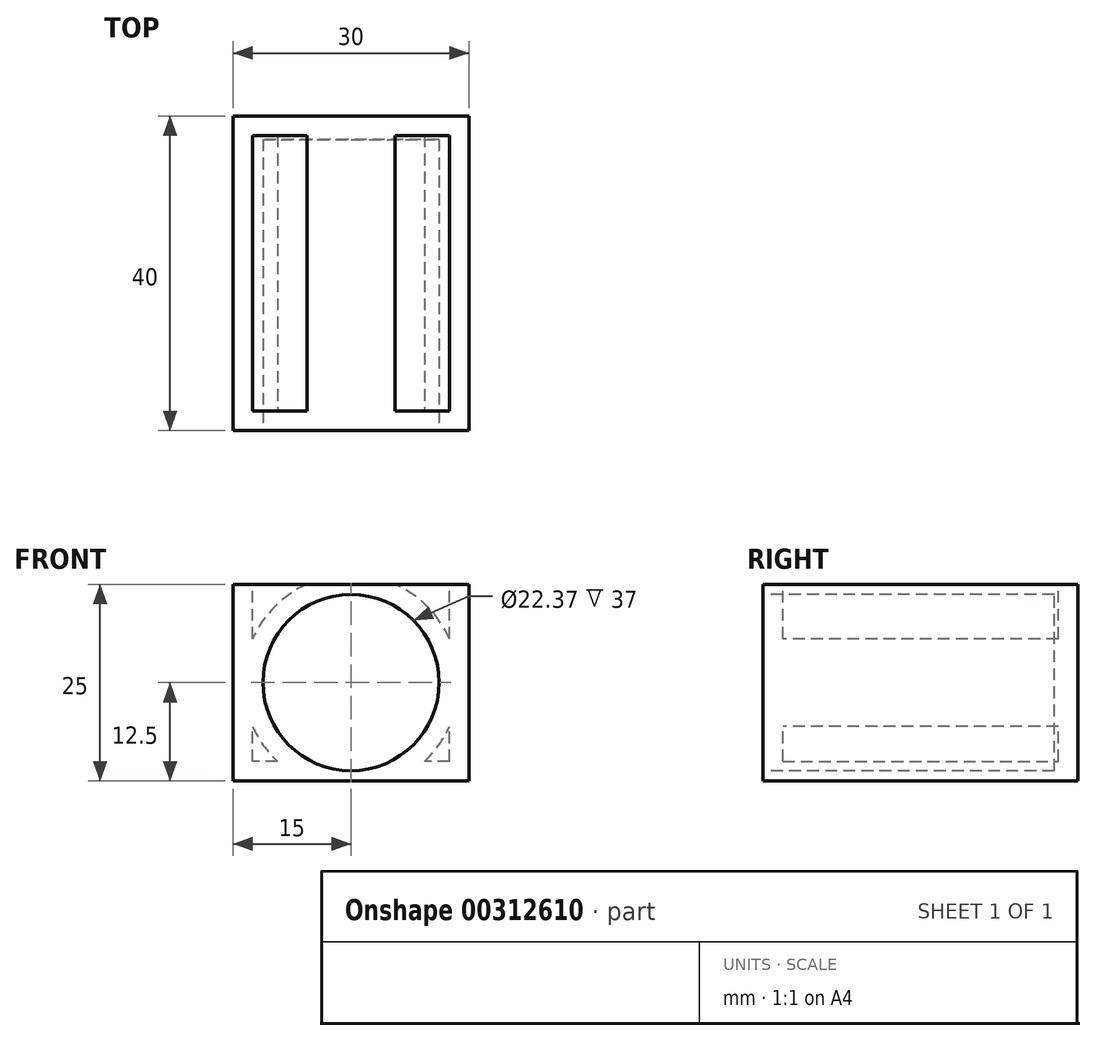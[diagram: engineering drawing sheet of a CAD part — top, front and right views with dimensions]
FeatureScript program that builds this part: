
annotation { "Feature Type Name" : "Feature", "Feature Type Description" : "" }
export const myFeature = defineFeature(function(context is Context, id is Id, definition is map)
    precondition{}
    {
        {
            var Q0;
            Q0=qCreatedBy(makeId("Front.planeOp"),FACE);
            var sketch = newSketch(context, id + "F0", { "sketchPlane" : qUnion([Q0])});
            skLineSegment(sketch, "E0.bottom", {"start": v(15, -12.5) * mm, "end": v(-15, -12.5) * mm});
            skLineSegment(sketch, "E0.top", {"start": v(15, 12.5) * mm, "end": v(-15, 12.5) * mm});
            skLineSegment(sketch, "E0.left", {"start": v(15, -12.5) * mm, "end": v(15, 12.5) * mm});
            skLineSegment(sketch, "E0.right", {"start": v(-15, -12.5) * mm, "end": v(-15, 12.5) * mm});
            skPoint(sketch, "E0.middle", {"position": v(0, 0) * mm});
            skSolve(sketch);
        }
        {
            var Q0;
            Q0=makeQuery(id+"F0.imprint","IMPRINT",FACE,{"disambiguationData":[TD([[makeQuery(id+"F0.imprint","IMPRINT",EDGE,{"derivedFrom":sQuery(id+"F0.wireOp",EDGE,"E0.bottom")}),-1.0]])]});
            extrude(context, id + "F1", {"entities" : qUnion([Q0]), "depth" : 40 * mm});
        }
        {
            var Q0;
            Q0=makeQuery(id+"F1.opExtrude","CAP_FACE",FACE,{"disambiguationData":[OSD([sQuery(id+"F0.wireOp",EDGE,"E0.bottom"),sQuery(id+"F0.wireOp",EDGE,"E0.top"),sQuery(id+"F0.wireOp",EDGE,"E0.left"),sQuery(id+"F0.wireOp",EDGE,"E0.right")])],"isStart":false});
            var sketch = newSketch(context, id + "F2", { "sketchPlane" : qUnion([Q0])});
            skCircle(sketch, "E1", {"center": v(0, 0) * mm, "radius": 11.19 * mm});
            skSolve(sketch);
        }
        {
            var Q0;
            Q0=makeQuery(id+"F2.imprint","IMPRINT",FACE,{"disambiguationData":[TD([[makeQuery(id+"F2.imprint","IMPRINT",EDGE,{"derivedFrom":sQuery(id+"F2.wireOp",EDGE,"E1")}),1.0]])]});
            extrude(context, id + "F3", {"entities" : qUnion([Q0]), "operationType" : NewBodyOperationType.REMOVE, "oppositeDirection" : true, "depth" : 37 * mm});
        }
        {
            var Q0;
            Q0=makeQuery(id+"F1.opExtrude","SWEPT_FACE",FACE,{"disambiguationData":[OSD([sQuery(id+"F0.wireOp",EDGE,"E0.top")])]});
            shell(context, id + "F4", {"entities" : qUnion([Q0]), "thickness" : 2.5 * mm});
        }
    });
